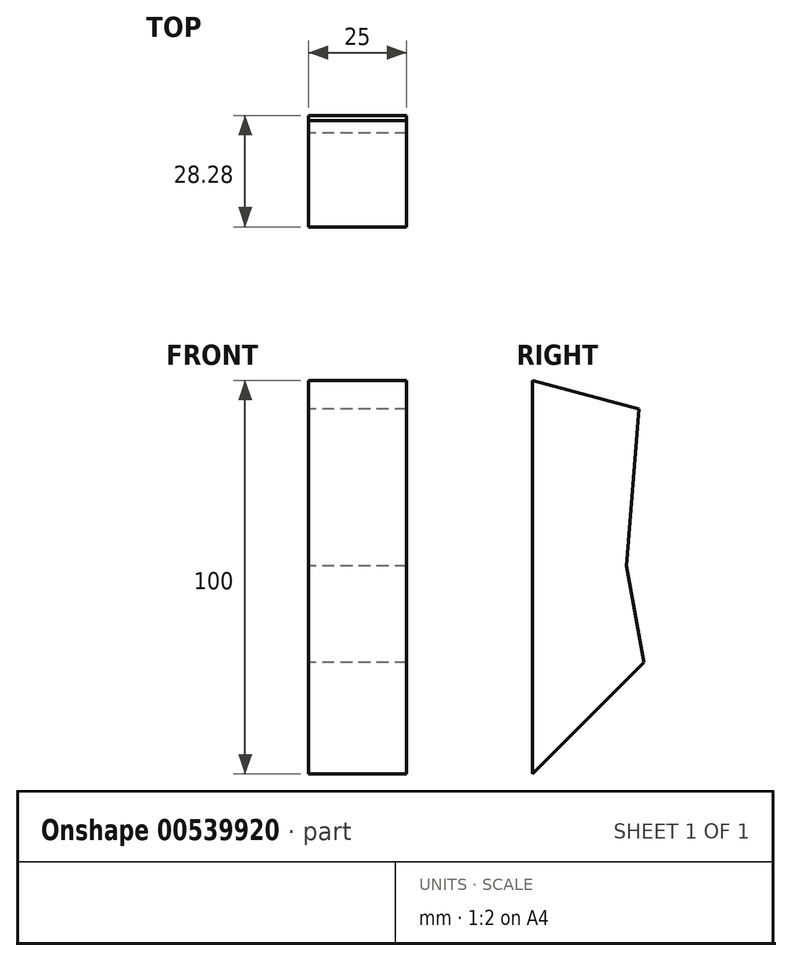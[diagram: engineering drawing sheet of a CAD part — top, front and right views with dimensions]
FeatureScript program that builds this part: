
annotation { "Feature Type Name" : "Feature", "Feature Type Description" : "" }
export const myFeature = defineFeature(function(context is Context, id is Id, definition is map)
    precondition{}
    {
        {
            var Q0;
            Q0=qCreatedBy(makeId("Right.planeOp"),FACE);
            var sketch = newSketch(context, id + "F0", { "sketchPlane" : qUnion([Q0])});
            skLineSegment(sketch, "E0", {"start": v(0, 0) * mm, "end": v(0, -100) * mm});
            skLineSegment(sketch, "E1", {"start": v(0, -100) * mm, "end": v(28.28, -71.72) * mm});
            skLineSegment(sketch, "E2", {"start": v(28.28, -71.72) * mm, "end": v(23.82, -47.12) * mm});
            skLineSegment(sketch, "E3", {"start": v(23.82, -47.12) * mm, "end": v(27.05, -7.25) * mm});
            skLineSegment(sketch, "E4", {"start": v(27.05, -7.25) * mm, "end": v(0, 0) * mm});
            skSolve(sketch);
        }
        {
            var Q0;
            Q0 = qSketchRegion(id + "F0", true);
            extrude(context, id + "F1", {"entities" : qUnion([Q0]), "endBound" : BoundingType.SYMMETRIC, "depth" : 25 * mm, "offsetDistance" : 25 * mm});
        }
    });
